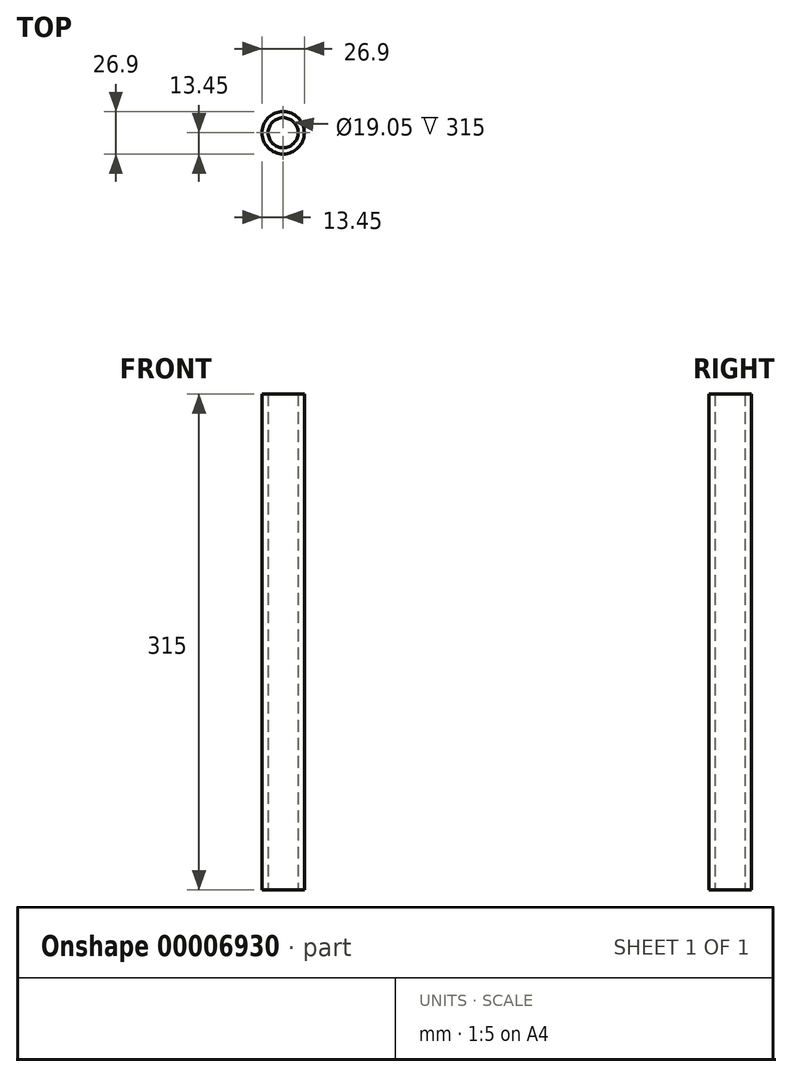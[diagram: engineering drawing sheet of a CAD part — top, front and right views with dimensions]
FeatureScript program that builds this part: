
annotation { "Feature Type Name" : "Feature", "Feature Type Description" : "" }
export const myFeature = defineFeature(function(context is Context, id is Id, definition is map)
    precondition{}
    {
        {
            var Q0;
            Q0=qCreatedBy(makeId("Top.planeOp"),FACE);
            var sketch = newSketch(context, id + "F0", { "sketchPlane" : qUnion([Q0])});
            skCircle(sketch, "E0", {"center": v(0, 0) * mm, "radius": 13.45 * mm});
            skCircle(sketch, "E1", {"center": v(0, 0) * mm, "radius": 9.53 * mm});
            skSolve(sketch);
        }
        {
            var Q0;
            Q0=makeQuery(id+"F0.imprint","IMPRINT",FACE,{"disambiguationData":[TD([[makeQuery(id+"F0.imprint","IMPRINT",EDGE,{"derivedFrom":sQuery(id+"F0.wireOp",EDGE,"E0")}),1.0]])]});
            extrude(context, id + "F1", {"entities" : qUnion([Q0]), "depth" : (315) * mm});
        }
    });
